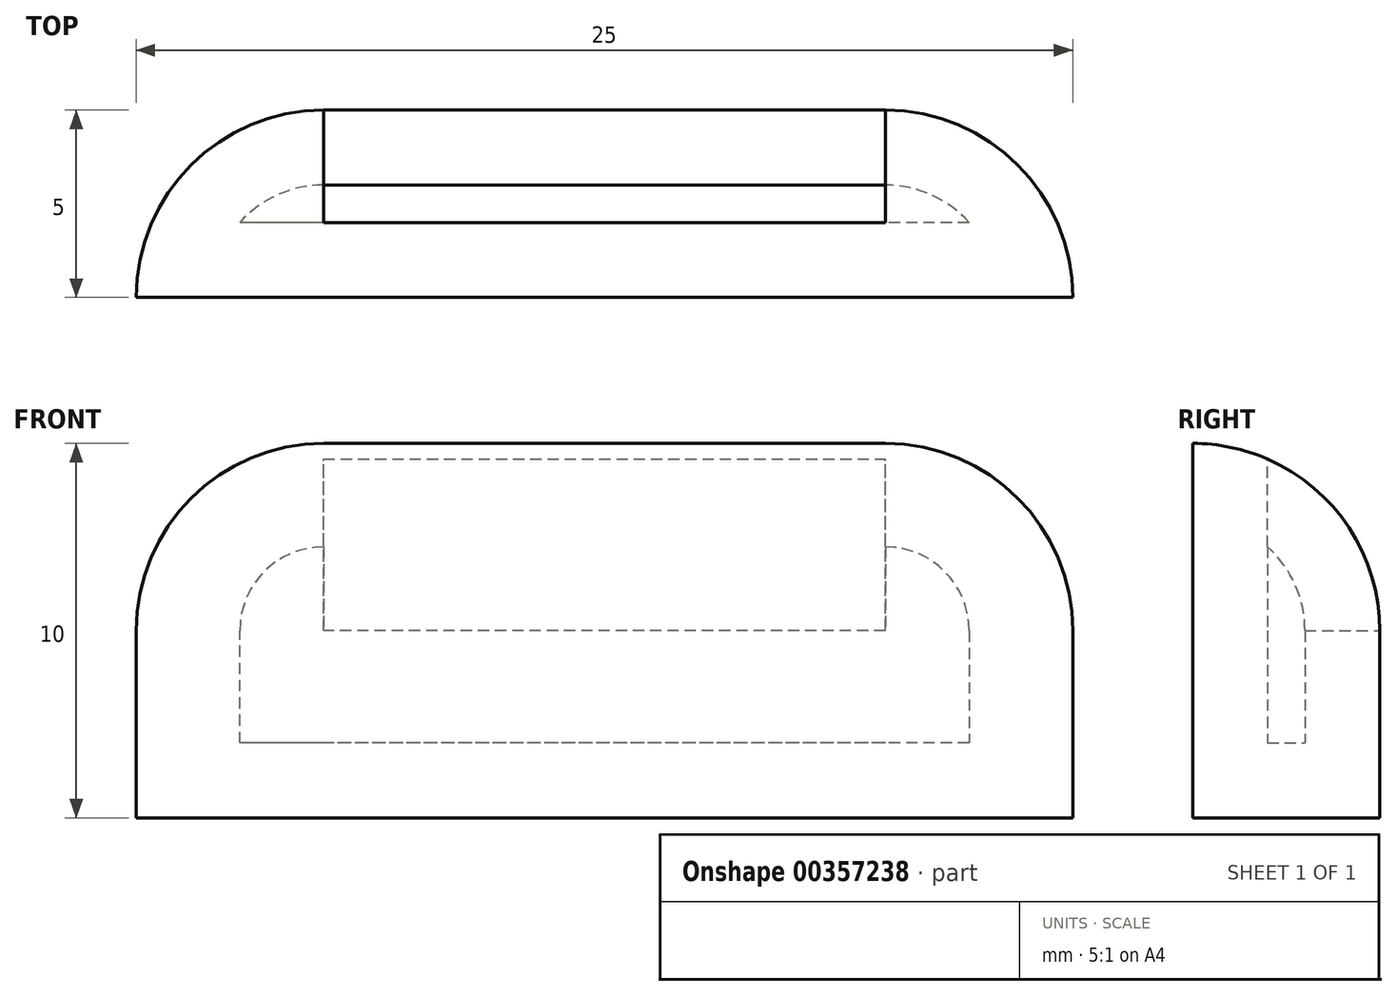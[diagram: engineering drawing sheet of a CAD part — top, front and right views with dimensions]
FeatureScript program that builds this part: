
annotation { "Feature Type Name" : "Feature", "Feature Type Description" : "" }
export const myFeature = defineFeature(function(context is Context, id is Id, definition is map)
    precondition{}
    {
        {
            var Q0;
            Q0=qCreatedBy(makeId("Top.planeOp"),FACE);
            var sketch = newSketch(context, id + "F0", { "sketchPlane" : qUnion([Q0])});
            skLineSegment(sketch, "E0.bottom", {"start": v(12.5, -2.5) * mm, "end": v(-12.5, -2.5) * mm});
            skLineSegment(sketch, "E0.top", {"start": v(12.5, 2.5) * mm, "end": v(-12.5, 2.5) * mm});
            skLineSegment(sketch, "E0.left", {"start": v(12.5, -2.5) * mm, "end": v(12.5, 2.5) * mm});
            skLineSegment(sketch, "E0.right", {"start": v(-12.5, -2.5) * mm, "end": v(-12.5, 2.5) * mm});
            skPoint(sketch, "E0.middle", {"position": v(0, 0) * mm});
            skSolve(sketch);
        }
        {
            var Q0;
            Q0 = qSketchRegion(id + "F0", true);
            extrude(context, id + "F1", {"entities" : qUnion([Q0]), "depth" : 10 * mm});
        }
        {
            var Q0;
            Q0=makeQuery(id+"F1.opExtrude","CAP_EDGE",EDGE,{"disambiguationData":[OSD([sQuery(id+"F0.wireOp",EDGE,"E0.right")])],"isStart":false});
            var Q1;
            Q1=makeQuery(id+"F1.opExtrude","CAP_EDGE",EDGE,{"disambiguationData":[OSD([sQuery(id+"F0.wireOp",EDGE,"E0.left")])],"isStart":false});
            var Q2;
            Q2=makeQuery(id+"F1.opExtrude","CAP_EDGE",EDGE,{"disambiguationData":[OSD([sQuery(id+"F0.wireOp",EDGE,"E0.top")])],"isStart":false});
            fillet(context, id + "F2", {"entities" : qUnion([Q0, Q1, Q2]), "radius" : 5 * mm, "tangentPropagation" : true, "allowEdgeOverflow" : false});
        }
        {
            var Q0;
            Q0=makeQuery(id+"F1.opExtrude","SWEPT_EDGE",EDGE,{"disambiguationData":[OSD([sQuery(id+"F0.wireOp",EDGE,"E0.top"),sQuery(id+"F0.wireOp",EDGE,"E0.left")])]});
            var Q1;
            Q1=makeQuery(id+"F1.opExtrude","SWEPT_EDGE",EDGE,{"disambiguationData":[OSD([sQuery(id+"F0.wireOp",EDGE,"E0.top"),sQuery(id+"F0.wireOp",EDGE,"E0.right")])]});
            fillet(context, id + "F3", {"entities" : qUnion([Q0, Q1]), "radius" : 5 * mm, "tangentPropagation" : true, "allowEdgeOverflow" : false});
        }
        {
            var Q0;
            Q0=makeQuery(id+"F2.opFillet","BLEND_FACE",FACE,{"disambiguationData":[OSD([sQuery(id+"F0.wireOp",EDGE,"E0.top")])]});
            shell(context, id + "F4", {"entities" : qUnion([Q0]), "thickness" : 2 * mm});
        }
    });
